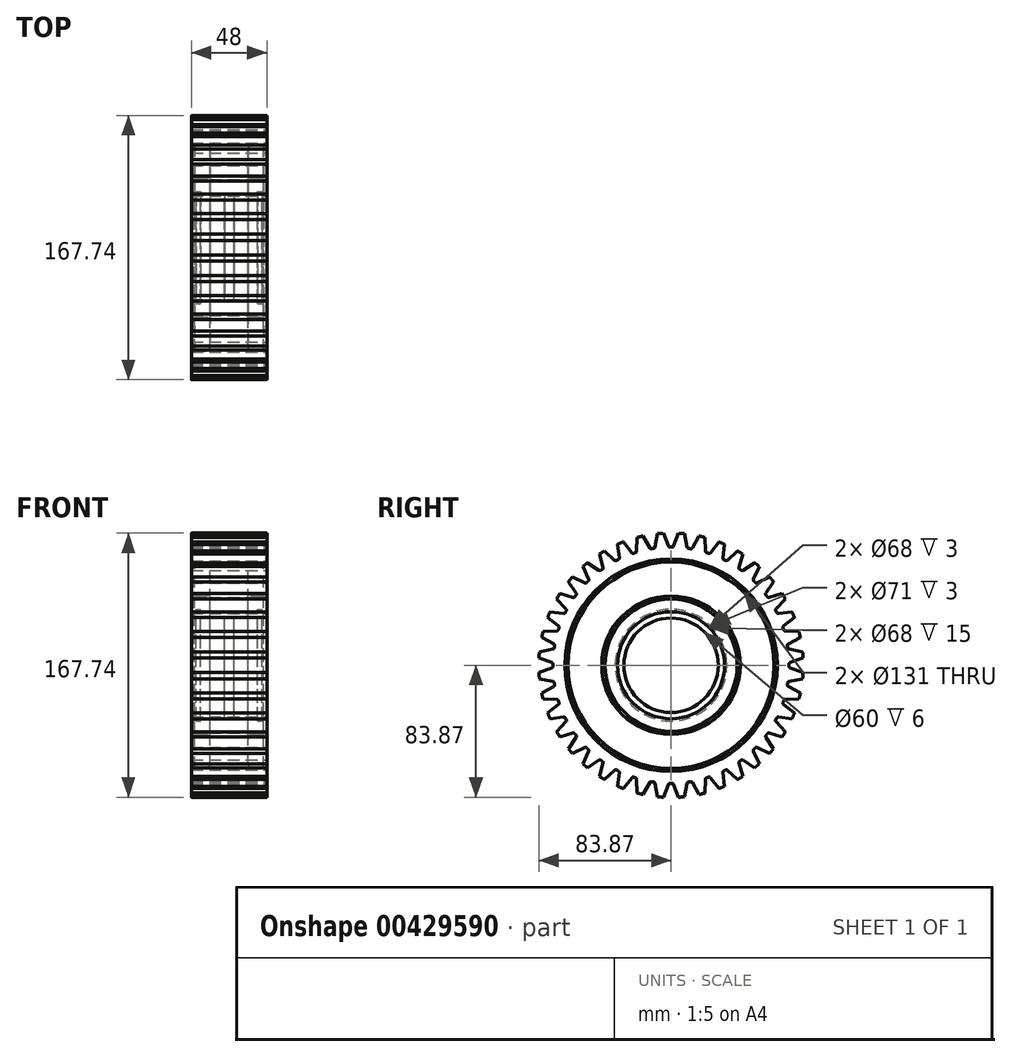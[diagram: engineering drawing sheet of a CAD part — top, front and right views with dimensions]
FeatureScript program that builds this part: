
annotation { "Feature Type Name" : "Feature", "Feature Type Description" : "" }
export const myFeature = defineFeature(function(context is Context, id is Id, definition is map)
    precondition{}
    {
        {
            var Q0;
            Q0=qCreatedBy(makeId("Front.planeOp"),FACE);
            var sketch = newSketch(context, id + "F0", { "sketchPlane" : qUnion([Q0])});
            skLineSegment(sketch, "E0.bottom", {"start": v(0, 0) * mm, "end": v(-24, 0) * mm, "construction": true});
            skLineSegment(sketch, "E0.top", {"start": v(0, 84) * mm, "end": v(-24, 84) * mm});
            skLineSegment(sketch, "E0.left", {"start": v(0, 0) * mm, "end": v(0, 84) * mm, "construction": true});
            skLineSegment(sketch, "E0.right", {"start": v(-24, 34) * mm, "end": v(-24, 44) * mm});
            skLineSegment(sketch, "E1", {"start": v(-24, 34) * mm, "end": v(-21, 34) * mm});
            skLineSegment(sketch, "E2", {"start": v(-21, 34) * mm, "end": v(-21, 35.5) * mm});
            skLineSegment(sketch, "E3", {"start": v(-21, 35.5) * mm, "end": v(-18, 35.5) * mm});
            skLineSegment(sketch, "E4", {"start": v(-18, 35.5) * mm, "end": v(-18, 34) * mm});
            skLineSegment(sketch, "E5", {"start": v(-18, 34) * mm, "end": v(-3, 34) * mm});
            skLineSegment(sketch, "E6", {"start": v(-3, 34) * mm, "end": v(-3, 30) * mm});
            skLineSegment(sketch, "E7", {"start": v(-3, 30) * mm, "end": v(0, 30) * mm});
            skLineSegment(sketch, "E8", {"start": v(-24, 44) * mm, "end": v(-15, 44) * mm});
            skLineSegment(sketch, "E9", {"start": v(-12, 47) * mm, "end": v(-12, 62.5) * mm});
            skLineSegment(sketch, "E10", {"start": v(-15, 65.5) * mm, "end": v(-24, 65.5) * mm});
            skLineSegment(sketch, "E11.trimOffspring", {"start": v(-24, 65.5) * mm, "end": v(-24, 84) * mm});
            skPoint(sketch, "E12.visualSharp", {"position": v(-12, 65.5) * mm});
            skArc(sketch, "E12.filletArc", {"start": v(-12, 62.5) * mm, "mid": v(-12.88, 64.62) * mm, "end": v(-15, 65.5) * mm});
            skPoint(sketch, "E13.visualSharp", {"position": v(-12, 44) * mm});
            skArc(sketch, "E13.filletArc", {"start": v(-15, 44) * mm, "mid": v(-12.88, 44.88) * mm, "end": v(-12, 47) * mm});
            skLineSegment(sketch, "E14.MirrorCS", {"start": v(0, 84) * mm, "end": v(24, 84) * mm});
            skLineSegment(sketch, "E15.MirrorCS", {"start": v(24, 65.5) * mm, "end": v(24, 84) * mm});
            skLineSegment(sketch, "E16.MirrorCS", {"start": v(15, 65.5) * mm, "end": v(24, 65.5) * mm});
            skArc(sketch, "E17.MirrorCS", {"start": v(12, 62.5) * mm, "mid": v(12.88, 64.62) * mm, "end": v(15, 65.5) * mm});
            skLineSegment(sketch, "E18.MirrorCS", {"start": v(12, 47) * mm, "end": v(12, 62.5) * mm});
            skArc(sketch, "E19.MirrorCS", {"start": v(15, 44) * mm, "mid": v(12.88, 44.88) * mm, "end": v(12, 47) * mm});
            skLineSegment(sketch, "E20.MirrorCS", {"start": v(24, 44) * mm, "end": v(15, 44) * mm});
            skLineSegment(sketch, "E21.MirrorCS", {"start": v(24, 34) * mm, "end": v(24, 44) * mm});
            skLineSegment(sketch, "E22.MirrorCS", {"start": v(24, 34) * mm, "end": v(21, 34) * mm});
            skLineSegment(sketch, "E23.MirrorCS", {"start": v(21, 34) * mm, "end": v(21, 35.5) * mm});
            skLineSegment(sketch, "E24.MirrorCS", {"start": v(21, 35.5) * mm, "end": v(18, 35.5) * mm});
            skLineSegment(sketch, "E25.MirrorCS", {"start": v(18, 35.5) * mm, "end": v(18, 34) * mm});
            skLineSegment(sketch, "E26.MirrorCS", {"start": v(18, 34) * mm, "end": v(3, 34) * mm});
            skLineSegment(sketch, "E27.MirrorCS", {"start": v(3, 34) * mm, "end": v(3, 30) * mm});
            skLineSegment(sketch, "E28.MirrorCS", {"start": v(3, 30) * mm, "end": v(0, 30) * mm});
            skSolve(sketch);
        }
        {
            var Q0;
            Q0=makeQuery(id+"F0.imprint","IMPRINT",FACE,{"disambiguationData":[TD([[makeQuery(id+"F0.imprint","IMPRINT",EDGE,{"derivedFrom":sQuery(id+"F0.wireOp",EDGE,"E0.top")}),1.0]])]});
            var Q1;
            Q1=sQuery(id+"F0.wireOp",EDGE,"E0.bottom");
            revolve(context, id + "F1", {"entities" : qUnion([Q0]), "axis" : qUnion([Q1]), "revolveType" : RevolveType.FULL});
        }
        {
            var Q0;
            Q0=qCreatedBy(makeId("Right.planeOp"),FACE);
            var sketch = newSketch(context, id + "F2", { "sketchPlane" : qUnion([Q0])});
            skArc(sketch, "E29", {"start": v(5, 84.85) * mm, "mid": v(0, 85) * mm, "end": v(-5, 84.85) * mm});
            skArc(sketch, "E30", {"start": v(0.7, 75) * mm, "mid": v(0, 75) * mm, "end": v(-0.7, 75) * mm});
            skLineSegment(sketch, "E31", {"start": v(0, 0) * mm, "end": v(0, 85) * mm, "construction": true});
            skLineSegment(sketch, "E32", {"start": v(-1.65, 75.65) * mm, "end": v(-5, 84.85) * mm});
            skLineSegment(sketch, "E33.MirrorCS", {"start": v(1.65, 75.65) * mm, "end": v(5, 84.85) * mm});
            skPoint(sketch, "E34.visualSharp", {"position": v(1.4, 74.99) * mm});
            skArc(sketch, "E34.filletArc", {"start": v(0.7, 75) * mm, "mid": v(1.28, 75.17) * mm, "end": v(1.65, 75.65) * mm});
            skPoint(sketch, "E35.visualSharp", {"position": v(-1.4, 74.99) * mm});
            skArc(sketch, "E35.filletArc", {"start": v(-1.65, 75.65) * mm, "mid": v(-1.28, 75.17) * mm, "end": v(-0.7, 75) * mm});
            skSolve(sketch);
        }
        {
            var Q0;
            Q0 = qSketchRegion(id + "F2", true);
            extrude(context, id + "F3", {"entities" : qUnion([Q0]), "operationType" : NewBodyOperationType.REMOVE, "endBound" : BoundingType.THROUGH_ALL, "oppositeDirection" : true, "depth" : 25 * mm, "hasSecondDirection" : true, "secondDirectionBound" : SecondDirectionBoundingType.THROUGH_ALL, "secondDirectionOppositeDirection" : false, "secondDirectionDepth" : 25 * mm});
        }
        {
            var Q0;
            Q0=makeQuery(id+"F3.boolean.opBoolean","COPY",FACE,{"derivedFrom":makeQuery(id+"F3.opExtrude","SWEPT_FACE",FACE,{"disambiguationData":[OSD([sQuery(id+"F2.wireOp",EDGE,"E33.MirrorCS")])]})});
            var Q1;
            Q1=makeQuery(id+"F3.boolean.opBoolean","COPY",FACE,{"derivedFrom":makeQuery(id+"F3.opExtrude","SWEPT_FACE",FACE,{"disambiguationData":[OSD([sQuery(id+"F2.wireOp",EDGE,"E30")])]})});
            var Q2;
            Q2=makeQuery(id+"F3.boolean.opBoolean","COPY",FACE,{"derivedFrom":makeQuery(id+"F3.opExtrude","SWEPT_FACE",FACE,{"disambiguationData":[OSD([sQuery(id+"F2.wireOp",EDGE,"E34.filletArc")])]})});
            var Q3;
            Q3=makeQuery(id+"F3.boolean.opBoolean","COPY",FACE,{"derivedFrom":makeQuery(id+"F3.opExtrude","SWEPT_FACE",FACE,{"disambiguationData":[OSD([sQuery(id+"F2.wireOp",EDGE,"E35.filletArc")])]})});
            var Q4;
            Q4=makeQuery(id+"F3.boolean.opBoolean","COPY",FACE,{"derivedFrom":makeQuery(id+"F3.opExtrude","SWEPT_FACE",FACE,{"disambiguationData":[OSD([sQuery(id+"F2.wireOp",EDGE,"E32")])]})});
            var Q5;
            Q5=makeQuery(id+"F1.opRevolve","SWEPT_FACE",FACE,{"disambiguationData":[OSD([sQuery(id+"F0.wireOp",EDGE,"E0.top"),sQuery(id+"F0.wireOp",EDGE,"E14.MirrorCS")])]});
            circularPattern(context, id + "F4", {"patternType" : PatternType.FACE, "faces" : qUnion([Q0, Q1, Q2, Q3, Q4]), "axis" : qUnion([Q5]), "angle" : 360 * degree, "instanceCount" : 40, "equalSpace" : true});
        }
        {
            var Q0;
            Q0=makeQuery(id+"F1.opRevolve","SWEPT_EDGE",EDGE,{"disambiguationData":[OSD([sQuery(id+"F0.wireOp",EDGE,"E10"),sQuery(id+"F0.wireOp",EDGE,"E11.trimOffspring")])]});
            var Q1;
            Q1=makeQuery(id+"F1.opRevolve","SWEPT_EDGE",EDGE,{"disambiguationData":[OSD([sQuery(id+"F0.wireOp",EDGE,"E0.right"),sQuery(id+"F0.wireOp",EDGE,"E8")])]});
            var Q2;
            Q2=makeQuery(id+"F1.opRevolve","SWEPT_EDGE",EDGE,{"disambiguationData":[OSD([sQuery(id+"F0.wireOp",EDGE,"E15.MirrorCS"),sQuery(id+"F0.wireOp",EDGE,"E16.MirrorCS")])]});
            var Q3;
            Q3=makeQuery(id+"F1.opRevolve","SWEPT_EDGE",EDGE,{"disambiguationData":[OSD([sQuery(id+"F0.wireOp",EDGE,"E20.MirrorCS"),sQuery(id+"F0.wireOp",EDGE,"E21.MirrorCS")])]});
            chamfer(context, id + "F5", {"entities" : qUnion([Q0, Q1, Q2, Q3]), "width" : 2 * mm, "tangentPropagation" : true});
        }
    });
